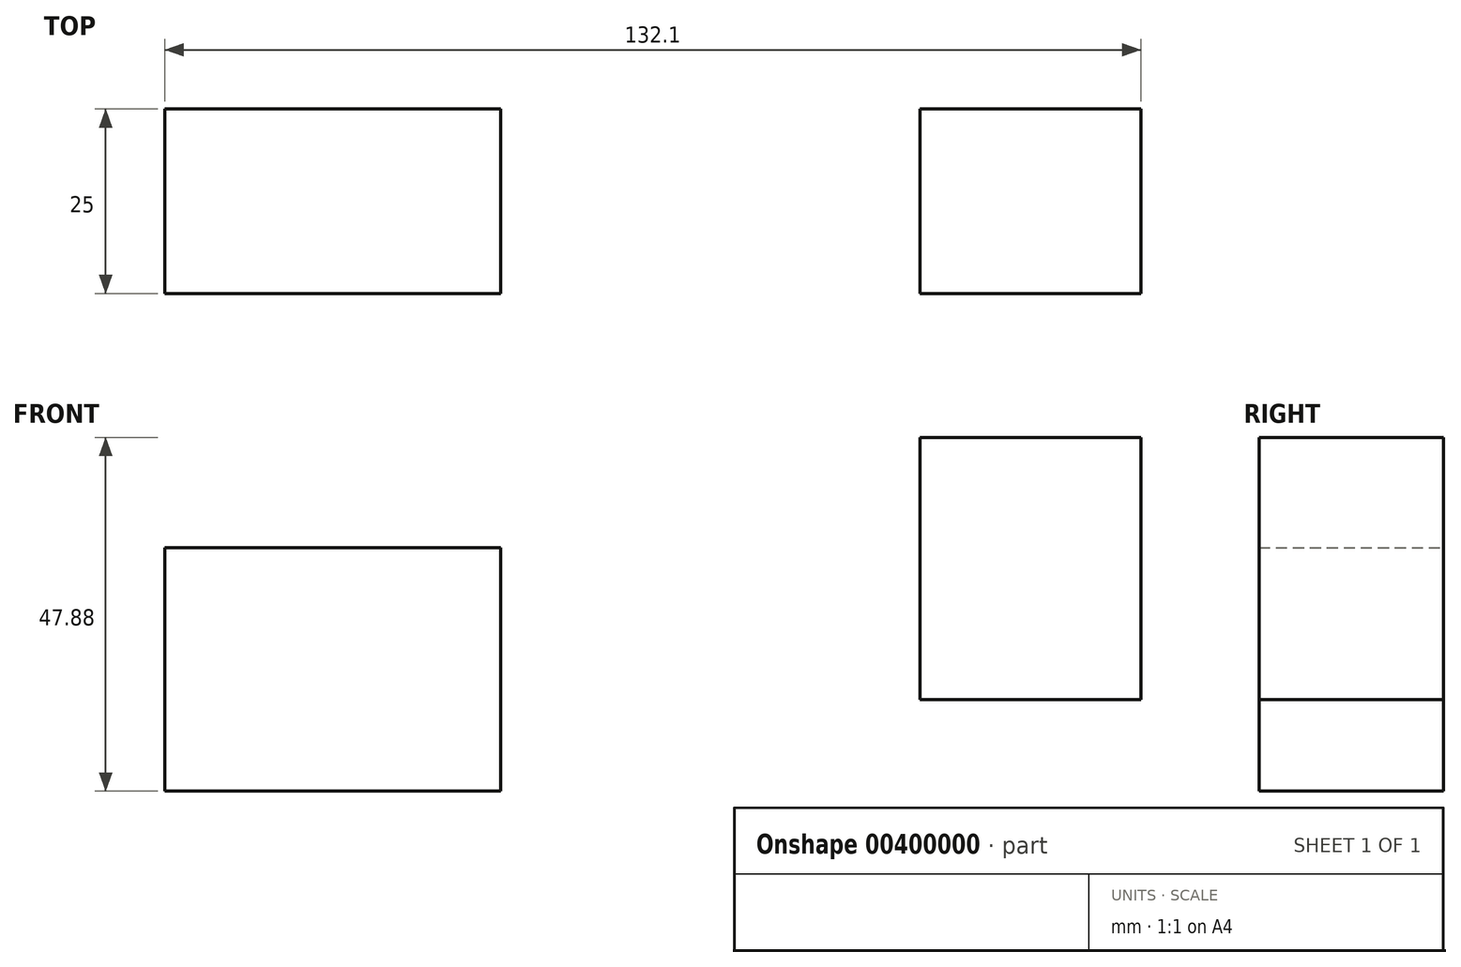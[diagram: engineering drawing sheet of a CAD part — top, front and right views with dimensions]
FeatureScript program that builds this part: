
annotation { "Feature Type Name" : "Feature", "Feature Type Description" : "" }
export const myFeature = defineFeature(function(context is Context, id is Id, definition is map)
    precondition{}
    {
        {
            var Q0;
            Q0=qCreatedBy(makeId("Front.planeOp"),FACE);
            var sketch = newSketch(context, id + "F0", { "sketchPlane" : qUnion([Q0])});
            skLineSegment(sketch, "E0.bottom", {"start": v(-193.44, 25.95) * mm, "end": v(-148, 25.95) * mm});
            skLineSegment(sketch, "E0.top", {"start": v(-193.44, -7.02) * mm, "end": v(-148, -7.02) * mm});
            skLineSegment(sketch, "E0.left", {"start": v(-193.44, 25.95) * mm, "end": v(-193.44, -7.02) * mm});
            skLineSegment(sketch, "E0.right", {"start": v(-148, 25.95) * mm, "end": v(-148, -7.02) * mm});
            skLineSegment(sketch, "E1.bottom", {"start": v(-91.2, 40.86) * mm, "end": v(-61.34, 40.86) * mm});
            skLineSegment(sketch, "E1.top", {"start": v(-91.2, 5.34) * mm, "end": v(-61.34, 5.34) * mm});
            skLineSegment(sketch, "E1.left", {"start": v(-91.2, 40.86) * mm, "end": v(-91.2, 5.34) * mm});
            skLineSegment(sketch, "E1.right", {"start": v(-61.34, 40.86) * mm, "end": v(-61.34, 5.34) * mm});
            skSolve(sketch);
        }
        {
            var Q0;
            Q0 = qSketchRegion(id + "F0", true);
            extrude(context, id + "F1", {"entities" : qUnion([Q0]), "depth" : 25 * mm});
        }
    });
